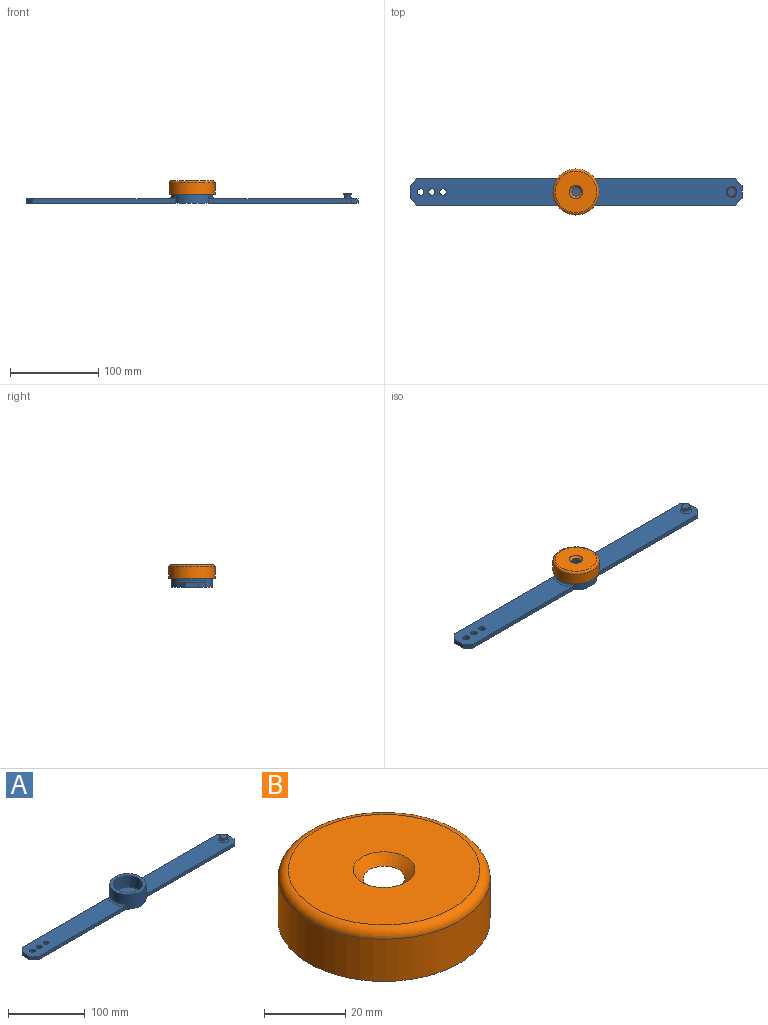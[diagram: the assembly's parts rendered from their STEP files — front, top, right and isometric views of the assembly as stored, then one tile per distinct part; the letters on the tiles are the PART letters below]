
ASSEMBLY  parts=2 mates=1
PART A: 27 faces, bbox 376.1x47.1x23.3 mm
  f0: cylinder r=23.55mm len=47.1mm, axis (0,0,-1), area 2955.4mm2, adj f1,f2,f5,f7,f9,f11,f17,f18
  f1: plane 376.1x47.1mm, normal (0,0,-1), area 11403.1mm2, adj f0,f5,f6,f7,f9,f10,f11,f13
  f2: plane 47.1x47.1mm, normal (0,0,1), area 602.2mm2, adj f0,f3
  f3: cylinder r=19.05mm len=38.1mm, axis (0,0,-1), area 2249.8mm2, adj f2,f4
  f4: plane 38.1x38.1mm, normal (0,0,1), area 1140.1mm2, adj f3
  f5: plane 162.19x7.62mm, normal (0,-1,0), area 825.7mm2, adj f0,f1,f8,f13,f17
  f6: plane 14.56x5.08mm, normal (1,0,0), area 74mm2, adj f1,f8,f13,f14
  f7: plane 162.19x7.62mm, normal (0,1,0), area 825.7mm2, adj f0,f1,f8,f14,f17
  f8: plane 166.63x29.8mm, normal (0,0,1), area 4696.3mm2, adj f5,f6,f7,f13,f14,f17,f26
  f9: plane 162.19x7.62mm, normal (0,1,0), area 825.7mm2, adj f0,f1,f12,f15,f18
  f10: plane 14.56x5.08mm, normal (-1,0,0), area 74mm2, adj f1,f12,f15,f16
  f11: plane 162.19x7.62mm, normal (0,-1,0), area 825.7mm2, adj f0,f1,f12,f16,f18
  f12: plane 166.63x29.8mm, normal (0,0,1), area 4685.3mm2, adj f9,f10,f11,f15,f16,f18,f19,f20
  f13: plane 7.62x7.62mm, normal (0.71,-0.71,0), area 54.7mm2, adj f1,f5,f6,f8
  f14: plane 7.62x7.62mm, normal (0.71,0.71,0), area 54.7mm2, adj f1,f6,f7,f8
  f15: plane 7.62x7.62mm, normal (-0.71,0.71,0), area 54.7mm2, adj f1,f9,f10,f12
  f16: plane 7.62x7.62mm, normal (-0.71,-0.71,0), area 54.7mm2, adj f1,f10,f11,f12
  f17: torus R=26.09mm, axis (0,0,1), area 127.9mm2, adj f0,f5,f7,f8
  f18: torus R=26.09mm, axis (0,0,1), area 127.9mm2, adj f0,f9,f11,f12
  f19: cylinder r=3.68mm len=7.37mm, axis (0,0,1), area 117.6mm2, adj f1,f12
  f20: cylinder r=3.68mm len=7.37mm, axis (0,0,1), area 117.6mm2, adj f1,f12
  f21: cylinder r=3.68mm len=7.37mm, axis (0,0,1), area 117.6mm2, adj f1,f12
  f22: cylinder r=3.56mm len=7.11mm, axis (0,0,-1), area 56.8mm2, adj f25,f26
  f23: cylinder r=4.83mm len=9.65mm, axis (0,0,-1), area 38.5mm2, adj f24,f25
  f24: plane 9.65x9.65mm, normal (0,0,1), area 73.2mm2, adj f23
  f25: plane 9.65x9.65mm, normal (0,0,-1), area 33.4mm2, adj f22,f23
  f26: torus R=6.1mm, axis (0,0,1), area 112.3mm2, adj f8,f22
PART B: 7 faces, bbox 56.5x56.5x15.2 mm
  f0: cylinder r=23.56mm len=47.12mm, axis (0,0,-1), area 1879.9mm2, adj f2,f3
  f1: cylinder r=26.1mm len=52.2mm, axis (0,0,-1), area 2082.6mm2, adj f2,f6
  f2: plane 52.2x52.2mm, normal (0,0,-1), area 396.2mm2, adj f0,f1
  f3: plane 47.12x47.12mm, normal (0,0,-1), area 1662.5mm2, adj f0,f5
  f4: plane 47.12x47.12mm, normal (0,0,1), area 1561.2mm2, adj f5,f6
  f5: cone r=5.08mm half-angle=45deg, axis (0,0,1), area 143.3mm2, adj f3,f4
  f6: torus R=23.56mm, axis (0,0,1), area 631.1mm2, adj f1,f4
PLACE A t=(14.37,-18.06,78.76)mm
PLACE B t=(14.37,-18.06,89.36)mm
MATE fastened B.f0 <-> A.f0  axis (0,0,-1) through (14.37,-18.06,102.06)mm
